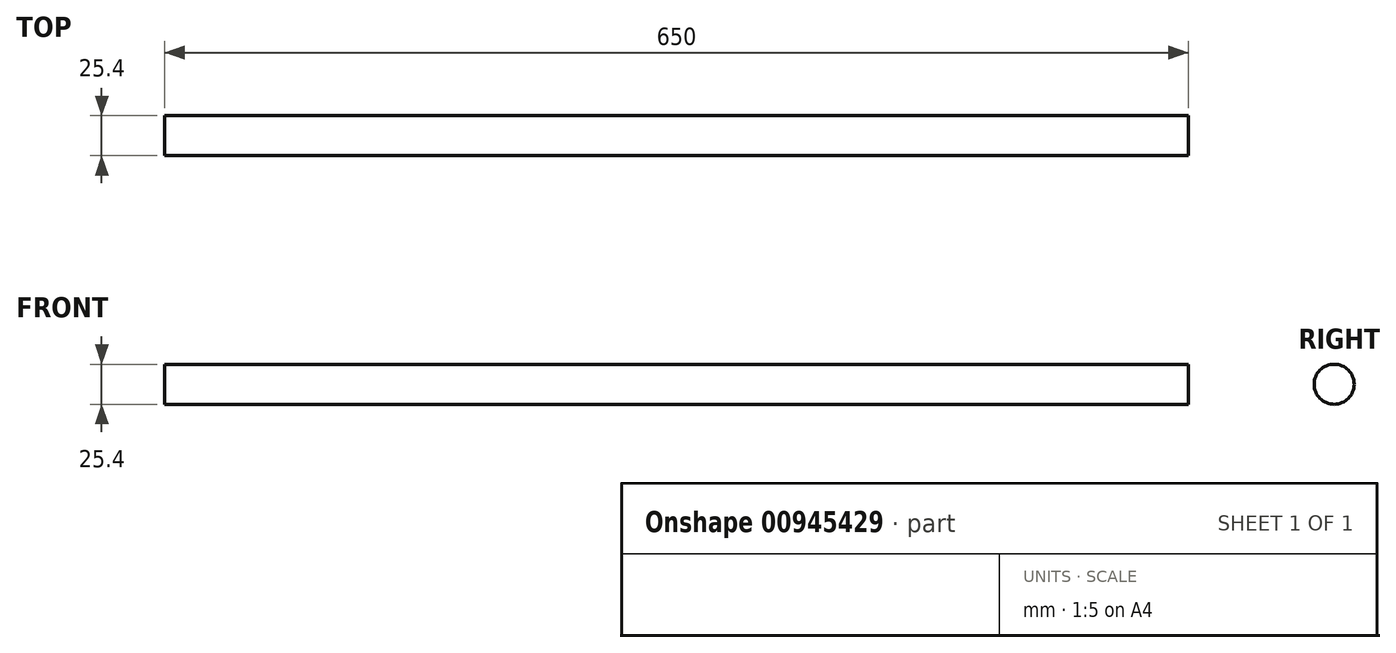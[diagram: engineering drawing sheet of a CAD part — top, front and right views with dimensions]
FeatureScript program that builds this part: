
annotation { "Feature Type Name" : "Feature", "Feature Type Description" : "" }
export const myFeature = defineFeature(function(context is Context, id is Id, definition is map)
    precondition{}
    {
        {
            var Q0;
            Q0=qCreatedBy(makeId("Right.planeOp"),FACE);
            var sketch = newSketch(context, id + "F0", { "sketchPlane" : qUnion([Q0])});
            skCircle(sketch, "E0", {"center": v(0, 0) * mm, "radius": 12.7 * mm});
            skSolve(sketch);
        }
        {
            var Q0;
            Q0=sQuery(id+"F0.wireOp",EDGE,"E0");
            extrude(context, id + "F1", {"bodyType" : ToolBodyType.SURFACE, "operationType" : NewBodyOperationType.INTERSECT, "surfaceEntities" : qUnion([Q0]), "depth" : 650 * mm, "offsetDistance" : 25.4 * mm});
        }
    });
